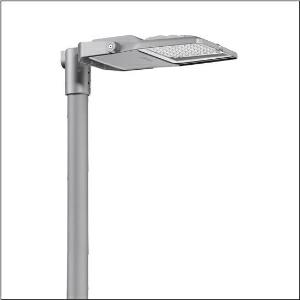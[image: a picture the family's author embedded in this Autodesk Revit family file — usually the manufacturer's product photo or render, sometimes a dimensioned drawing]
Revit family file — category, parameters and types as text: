
# Revit family: floodlight_fl_21_iq_mini___pl43_5xa7771d4a3a_2bc1
name_source: partatom
category: Lighting Fixtures
units: mm (PartAtom-declared; Revit-internal decimal feet)

## family parameters
Cut with Voids When Loaded = No
Host = Face
Light Source = No
Part Type = Normal
Room Calculation Point = No
Round Connector Dimension = Use Diameter
Shared = No

## types (1)
- --- (1 x LED, 19090 lm, 143 W, 4000K)
    Apparent Load = 143 VA
    CIE Flux Codes = 27 78 99 100 100
    Color Rendering = 70
    Color Temperature = 4000K
    Default Elevation = 1800 mm
    Description = Floodlight FL 21 iQ mini, floodlight, primary light control with lens, of PMMA, primary optical cover: protective disc, of toughened safety glass, transparent, light distribution: PL43, light emission: direct distribution, installation type: surface-mounted, LED, High Power LED, rated luminous flux: 19.090lm, luminous efficacy: 134lm/W, light colour: 740, colour temperature: 4000K, control: Auto-Match, Temp-Guard, Lumen-Switch, Night-Set, Smart-Wire, Light-Fading, Desk-Remote (wireless, voltage-free reading and setting of iQ features in the workshop via application-optimized NFC function/RFID function), optimised constant luminous flux control (CLO 2.0), with terminal, 6-pole, mains connection: 220..240V, AC, 50/60Hz, start of lifetime: 143W, end of service life: 152W, reduction: 61W, luminaire housing, of diecast aluminium, powder-coated, Siteco® metallic grey (DB 702S), corrosivity category C5 mid according to DIN EN ISO 12944, sealing non-destructively replaceable, please order mast flange separately, mast bracket, of steel, galvanised, powder-coated, Siteco® metallic grey (DB 702S), protection rating (complete): IP66, insulation class (complete): insulation class II (safety insulation), certification: CE, ENEC, VDE, protection symbol: D, impact resistance: IK08, permissible operating ambient temperature: -40..+40°C, permissible operating ambient temperature for outdoor applications: -40..+50°C, standard: DIN EN 12944, LABS conformity tested according to VDMA 24364:2018-05, packaging unit: 1 piece

Light Distribution: PL43
    Height = 70 mm
    Lamp = 1 x LED
    Lamp Light Flux = 19090 lm
    Lamp Power = 143 W
    Lamp count = 1
    Length = 485 mm
    Luminous efficacy = 133 lm/W
    Manufacturer = Siteco
    ModVariant = No
    Model = 5XA7771D4A3A
    Number of Poles = 1
    OnlyDefault = Yes
    Power Factor = 1
    Product Name = Floodlight FL 21 iQ mini | PL43
    Product group = floodlight | pylon annexe
    ProductGroupID = 6200
    Protection Class = Protection class II
    Protection Degree = IP 66
    RLX_Detail_Level = 1
    RLX_Emergency_Light_Flux = 0 lm
    RLX_Emergency_Type = 0
    RLX_Emergency_Type_DB = No
    RlxData = <blob elided: 101493 chars, md5=9abee663>
    Socket = socket
    Standby Power = 0 W
    System Light Flux = 19090 lm
    System Power = 143 W
    Type Comments = factory setting: luminous flux: 100 % | dim-lin: 254 | 730 mA
    Type Image = l_1007125.jpg
    URL = http://relux.com
    VarID = @adj_094053
    Voltage = 0 V
    Weight = 0.00 kg
    Width = 337 mm

## geometry (parser evidence)
native form markers: Blend x4, Sweep x11
no freeform markers — native parametric forms only
